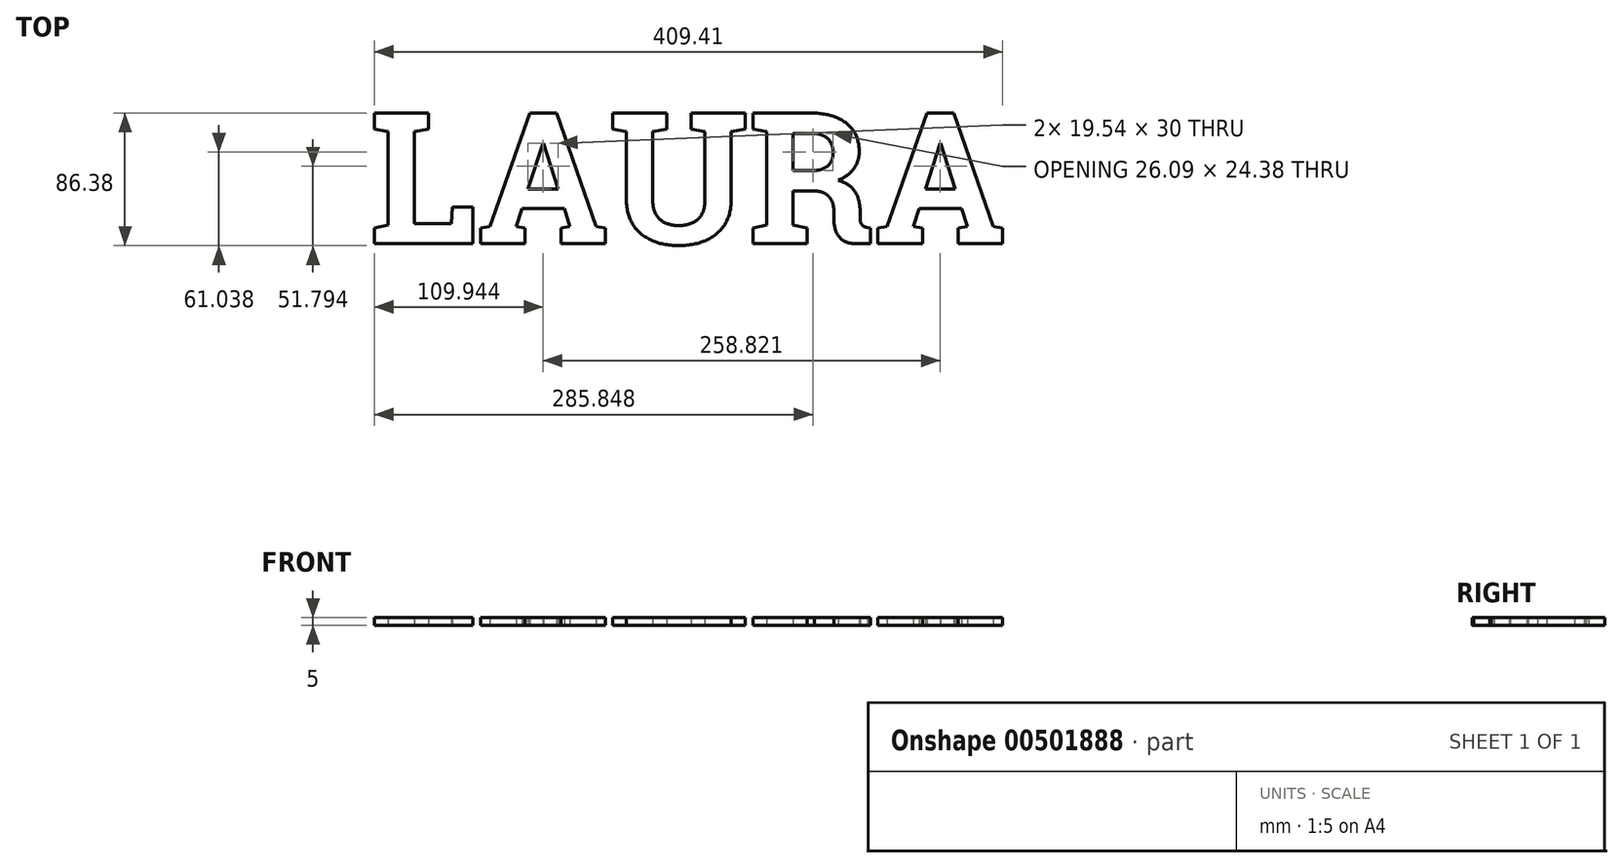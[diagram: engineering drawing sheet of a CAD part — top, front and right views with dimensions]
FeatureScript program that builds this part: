
annotation { "Feature Type Name" : "Feature", "Feature Type Description" : "" }
export const myFeature = defineFeature(function(context is Context, id is Id, definition is map)
    precondition{}
    {
        {
            var Q0;
            Q0=qCreatedBy(makeId("Top.planeOp"),FACE);
            var sketch = newSketch(context, id + "F0", { "sketchPlane" : qUnion([Q0])});
            skText(sketch, "E0", { "text": "LAURA", "fontName": "RobotoSlab-Bold.ttf"});
            const initialGuessF0  = {"E0": [-0.1846, 0, 1, 0, 0.08623]};
            skSetInitialGuess(sketch, initialGuessF0);
            skSolve(sketch);
        }
        {
            var Q0;
            Q0 = qSketchRegion(id + "F0", true);
            extrude(context, id + "F1", {"entities" : qUnion([Q0]), "depth" : 5 * mm});
        }
    });
